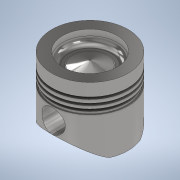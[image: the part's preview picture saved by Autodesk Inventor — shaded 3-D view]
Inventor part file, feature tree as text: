
AUTODESK INVENTOR PART (.ipt)
format: ipt  version: 2021 (Build 250183000, 183)  size: 299,008 bytes
history: native  units: mm
features: sketch x4, extrude x3, other x2, revolve x2, mirror x1
ambient origin geometry x8: Origin, YZ Plane, XZ Plane, XY Plane, X Axis, Y Axis, Z Axis, Center Point
bodies: Body1 (feature_tree)
feature tree (12):
  other  "Твердое тело1"
  revolve  "Вращение1"
  revolve  "Вращение2"
  extrude  "Выдавливание1"  Depth=80.0mm
  other  "РабПлоскость1"
  extrude  "Выдавливание2"  Depth=45.55mm
  mirror  "Зеркальное отражение1"
  extrude  "Выдавливание3"  Depth=13.0mm
  sketch  "Эскиз2"
  sketch  "Эскиз3"
  sketch  "Эскиз4"
  sketch  "Эскиз5"
